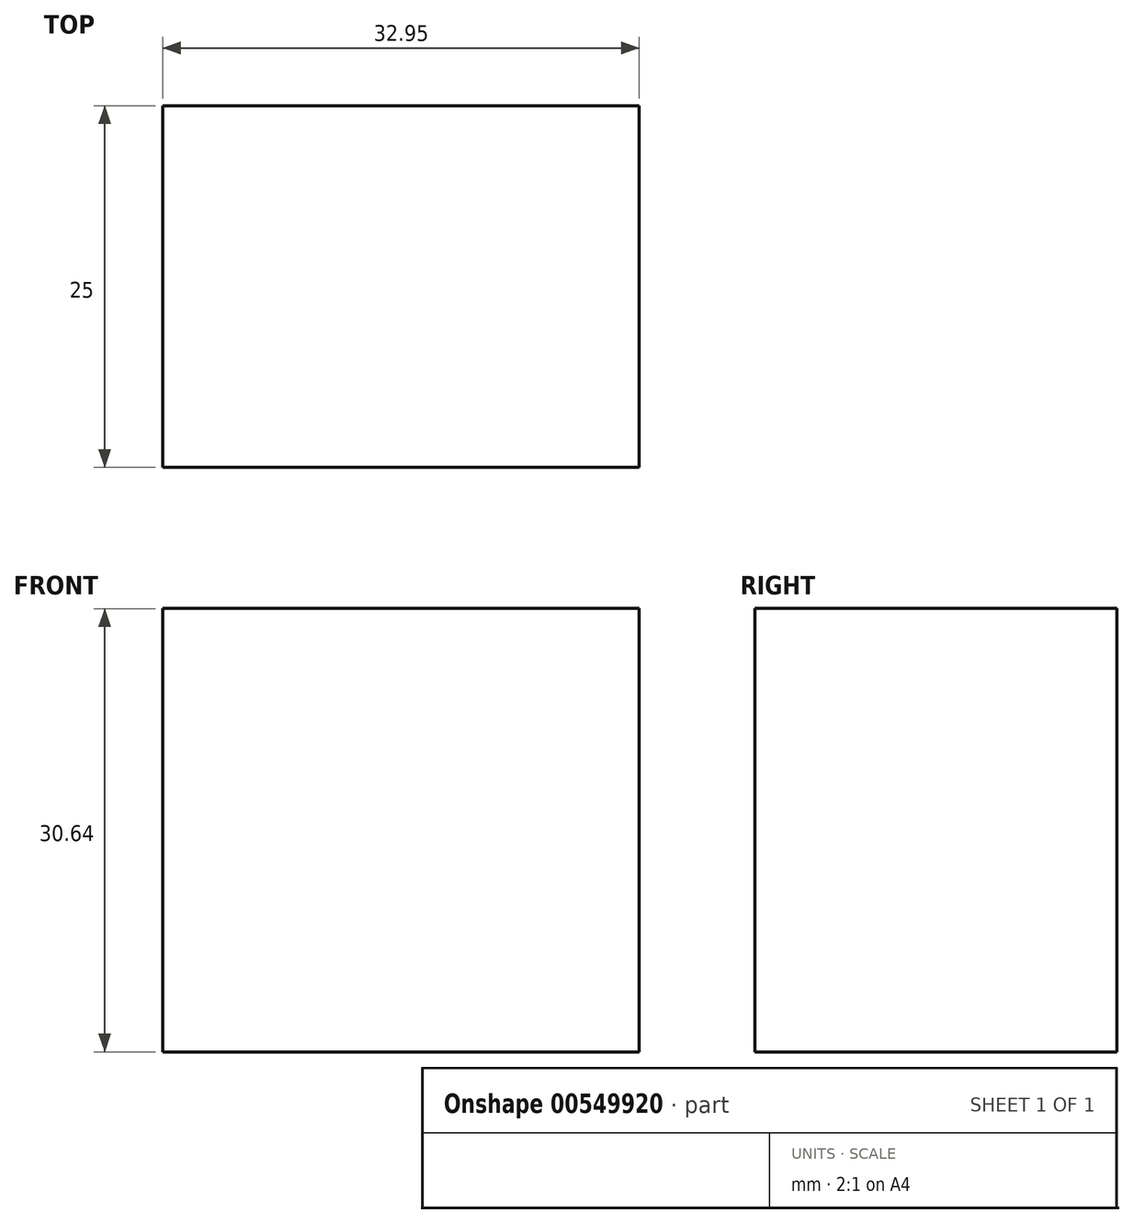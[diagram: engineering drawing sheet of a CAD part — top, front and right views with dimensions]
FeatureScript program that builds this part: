
annotation { "Feature Type Name" : "Feature", "Feature Type Description" : "" }
export const myFeature = defineFeature(function(context is Context, id is Id, definition is map)
    precondition{}
    {
        {
            var Q0;
            Q0=qCreatedBy(makeId("Front.planeOp"),FACE);
            var sketch = newSketch(context, id + "F0", { "sketchPlane" : qUnion([Q0])});
            skLineSegment(sketch, "E0.bottom", {"start": v(-141.64, 39.9) * mm, "end": v(-108.69, 39.9) * mm});
            skLineSegment(sketch, "E0.top", {"start": v(-141.64, 70.53) * mm, "end": v(-108.69, 70.53) * mm});
            skLineSegment(sketch, "E0.left", {"start": v(-141.64, 39.9) * mm, "end": v(-141.64, 70.53) * mm});
            skLineSegment(sketch, "E0.right", {"start": v(-108.69, 39.9) * mm, "end": v(-108.69, 70.53) * mm});
            skPoint(sketch, "E0.middle", {"position": v(-125.17, 55.21) * mm});
            skSolve(sketch);
        }
        {
            var Q0;
            Q0 = qSketchRegion(id + "F0", true);
            extrude(context, id + "F1", {"entities" : qUnion([Q0]), "depth" : 25 * mm, "offsetDistance" : 25 * mm});
        }
    });
